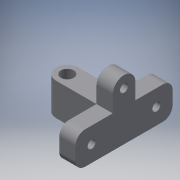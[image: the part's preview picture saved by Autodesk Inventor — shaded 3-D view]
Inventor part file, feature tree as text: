
AUTODESK INVENTOR PART (.ipt)
format: ipt  version: 2017 (Build 210142000, 142)  size: 152,064 bytes
history: native  units: mm
features: extrude x3, sketch x3, fillet x1
ambient origin geometry x8: Origin, YZ Plane, XZ Plane, XY Plane, X Axis, Y Axis, Z Axis, Center Point
bodies: Solid1 (feature_tree)
feature tree (7):
  extrude  "Extrusion1"  Depth=15.0mm
  extrude  "Extrusion2"  Depth=10.0mm
  fillet  "Fillet1"  Radius=7.0mm
  extrude  "Extrusion3"  Depth=10.0mm
  sketch  "Sketch1"  dims[d0=8.0mm d1=15.0mm]
  sketch  "Sketch2"  dims[d2=50.0mm d3=10.0mm d4=7.0mm]
  sketch  "Sketch3"  dims[d5=20.0mm d6=0.0mm d7=5.0mm d8=10.0mm d9=20.0mm d10=0.0mm d11=6.0mm d12=5.0mm d13=7.0mm d14=10.0mm d15=10.0mm d16=0.0mm]
